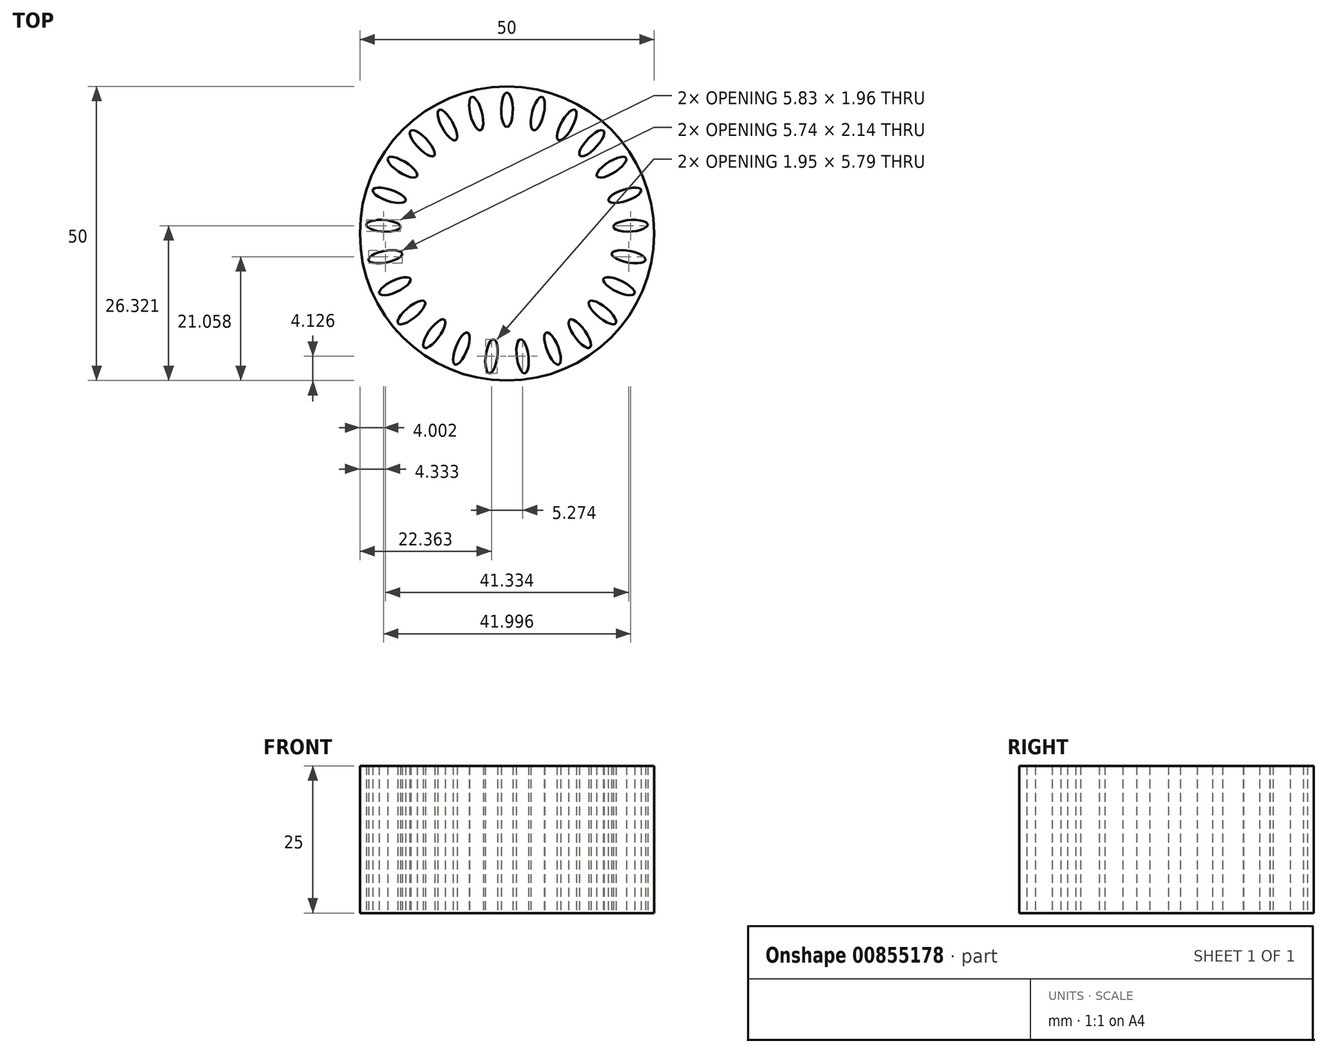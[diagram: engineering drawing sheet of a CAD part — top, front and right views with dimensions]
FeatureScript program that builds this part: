
annotation { "Feature Type Name" : "Feature", "Feature Type Description" : "" }
export const myFeature = defineFeature(function(context is Context, id is Id, definition is map)
    precondition{}
    {
        {
            var Q0;
            Q0=qCreatedBy(makeId("Top.planeOp"),FACE);
            var sketch = newSketch(context, id + "F0", { "sketchPlane" : qUnion([Q0])});
            skCircle(sketch, "E0", {"center": v(0, 0) * mm, "radius": 25 * mm});
            skEllipse(sketch, "E1", {"center": v(0, 21.04) * mm, "majorRadius": 2.92 * mm, "minorRadius": 0.98 * mm, "majorAxis": v(0, -1)});
            skEllipse(sketch, "E2.1.0", {"center": v(-5.23, 20.38) * mm, "majorRadius": 2.92 * mm, "minorRadius": 0.98 * mm, "majorAxis": v(0.25, -0.97)});
            skEllipse(sketch, "E2.2.0", {"center": v(-10.14, 18.44) * mm, "majorRadius": 2.92 * mm, "minorRadius": 0.98 * mm, "majorAxis": v(0.48, -0.88)});
            skEllipse(sketch, "E3.1.3.0", {"center": v(-14.4, 15.34) * mm, "majorRadius": 2.92 * mm, "minorRadius": 0.98 * mm, "majorAxis": v(0.68, -0.73)});
            skEllipse(sketch, "E3.1.4.0", {"center": v(-17.76, 11.27) * mm, "majorRadius": 2.92 * mm, "minorRadius": 0.98 * mm, "majorAxis": v(0.84, -0.54)});
            skEllipse(sketch, "E3.1.5.0", {"center": v(-20, 6.5) * mm, "majorRadius": 2.92 * mm, "minorRadius": 0.98 * mm, "majorAxis": v(0.95, -0.3)});
            skEllipse(sketch, "E3.1.6.0", {"center": v(-21, 1.32) * mm, "majorRadius": 2.92 * mm, "minorRadius": 0.98 * mm, "majorAxis": v(1, -0.06)});
            skEllipse(sketch, "E3.1.7.0", {"center": v(-20.67, -3.94) * mm, "majorRadius": 2.92 * mm, "minorRadius": 0.98 * mm, "majorAxis": v(0.98, 0.19)});
            skEllipse(sketch, "E3.1.8.0", {"center": v(-19.04, -8.96) * mm, "majorRadius": 2.92 * mm, "minorRadius": 0.98 * mm, "majorAxis": v(0.9, 0.43)});
            skEllipse(sketch, "E3.1.9.0", {"center": v(-16.21, -13.41) * mm, "majorRadius": 2.92 * mm, "minorRadius": 0.98 * mm, "majorAxis": v(0.77, 0.64)});
            skEllipse(sketch, "E3.1.10.0", {"center": v(-12.37, -17.02) * mm, "majorRadius": 2.92 * mm, "minorRadius": 0.98 * mm, "majorAxis": v(0.59, 0.8)});
            skEllipse(sketch, "E3.1.11.0", {"center": v(-7.75, -19.56) * mm, "majorRadius": 2.92 * mm, "minorRadius": 0.98 * mm, "majorAxis": v(0.37, 0.93)});
            skEllipse(sketch, "E3.1.12.0", {"center": v(-2.64, -20.87) * mm, "majorRadius": 2.92 * mm, "minorRadius": 0.98 * mm, "majorAxis": v(0.13, 1)});
            skEllipse(sketch, "E3.1.13.0", {"center": v(2.64, -20.87) * mm, "majorRadius": 2.92 * mm, "minorRadius": 0.98 * mm, "majorAxis": v(-0.13, 1)});
            skEllipse(sketch, "E3.1.14.0", {"center": v(7.75, -19.56) * mm, "majorRadius": 2.92 * mm, "minorRadius": 0.98 * mm, "majorAxis": v(-0.37, 0.93)});
            skEllipse(sketch, "E3.1.15.0", {"center": v(12.37, -17.02) * mm, "majorRadius": 2.92 * mm, "minorRadius": 0.98 * mm, "majorAxis": v(-0.59, 0.8)});
            skEllipse(sketch, "E3.1.16.0", {"center": v(16.21, -13.41) * mm, "majorRadius": 2.92 * mm, "minorRadius": 0.98 * mm, "majorAxis": v(-0.77, 0.64)});
            skEllipse(sketch, "E3.1.17.0", {"center": v(19.04, -8.96) * mm, "majorRadius": 2.92 * mm, "minorRadius": 0.98 * mm, "majorAxis": v(-0.9, 0.43)});
            skEllipse(sketch, "E3.1.18.0", {"center": v(20.67, -3.94) * mm, "majorRadius": 2.92 * mm, "minorRadius": 0.98 * mm, "majorAxis": v(-0.98, 0.19)});
            skEllipse(sketch, "E3.1.19.0", {"center": v(21, 1.32) * mm, "majorRadius": 2.92 * mm, "minorRadius": 0.98 * mm, "majorAxis": v(-1, -0.06)});
            skEllipse(sketch, "E3.1.20.0", {"center": v(20, 6.5) * mm, "majorRadius": 2.92 * mm, "minorRadius": 0.98 * mm, "majorAxis": v(-0.95, -0.3)});
            skEllipse(sketch, "E3.1.21.0", {"center": v(17.76, 11.27) * mm, "majorRadius": 2.92 * mm, "minorRadius": 0.98 * mm, "majorAxis": v(-0.84, -0.54)});
            skEllipse(sketch, "E3.1.22.0", {"center": v(14.4, 15.34) * mm, "majorRadius": 2.92 * mm, "minorRadius": 0.98 * mm, "majorAxis": v(-0.68, -0.73)});
            skEllipse(sketch, "E3.1.23.0", {"center": v(10.14, 18.44) * mm, "majorRadius": 2.92 * mm, "minorRadius": 0.98 * mm, "majorAxis": v(-0.48, -0.88)});
            skEllipse(sketch, "E3.1.24.0", {"center": v(5.23, 20.38) * mm, "majorRadius": 2.92 * mm, "minorRadius": 0.98 * mm, "majorAxis": v(-0.25, -0.97)});
            skSolve(sketch);
        }
        {
            var Q0;
            Q0=makeQuery(id+"F0.imprint","IMPRINT",FACE,{"disambiguationData":[TD([[makeQuery(id+"F0.imprint","IMPRINT",EDGE,{"derivedFrom":sQuery(id+"F0.wireOp",EDGE,"E0")}),1.0]])]});
            extrude(context, id + "F1", {"entities" : qUnion([Q0]), "depth" : 25 * mm, "offsetDistance" : 25 * mm});
        }
    });
